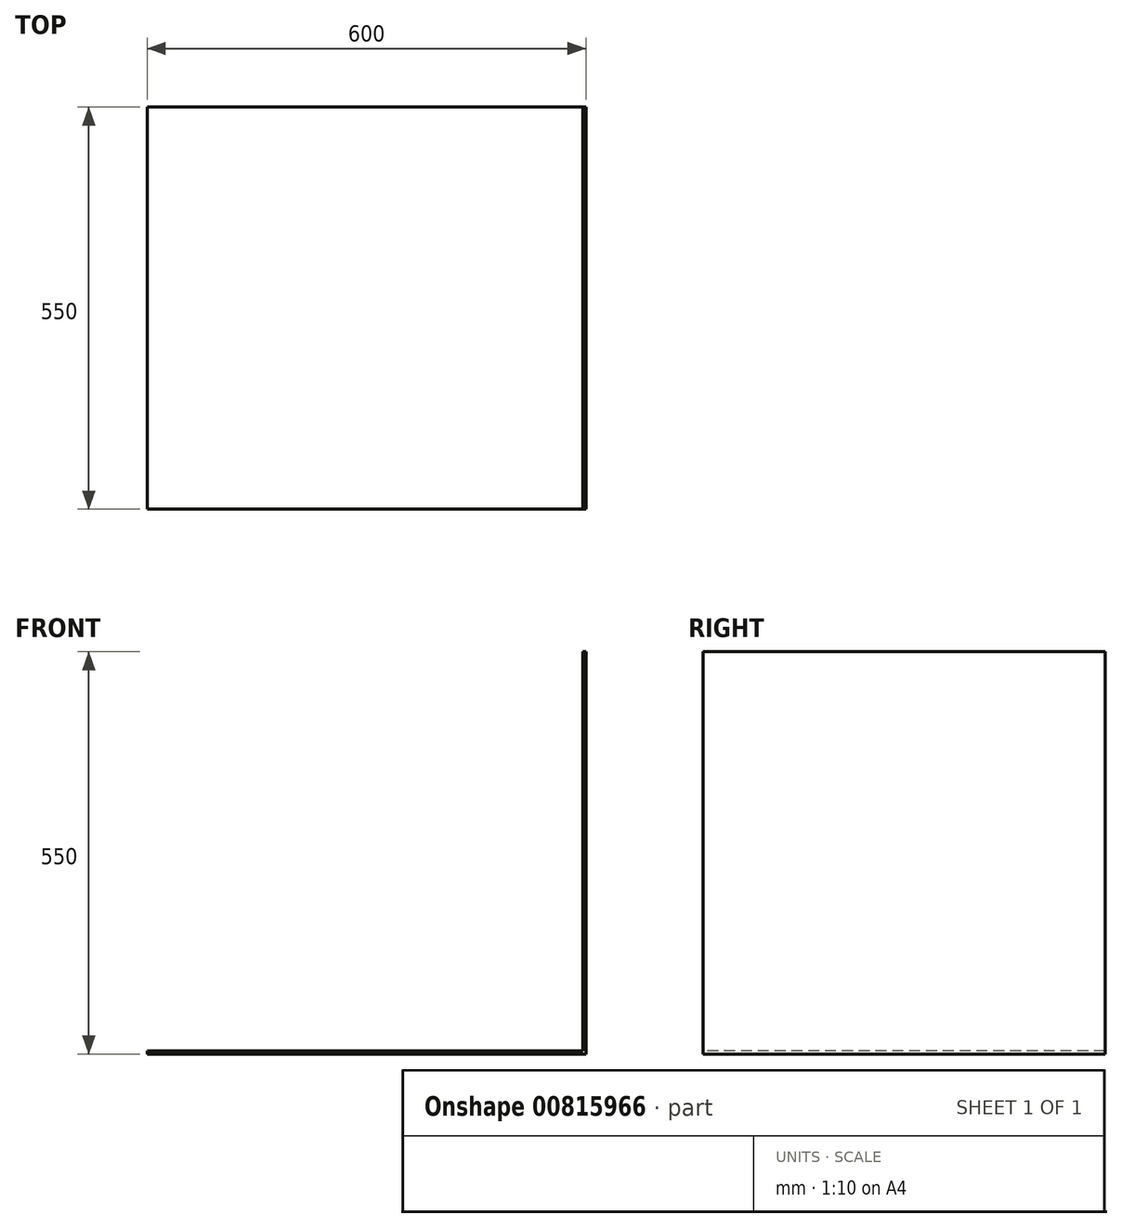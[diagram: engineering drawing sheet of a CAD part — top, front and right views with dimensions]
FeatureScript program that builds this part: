
annotation { "Feature Type Name" : "Feature", "Feature Type Description" : "" }
export const myFeature = defineFeature(function(context is Context, id is Id, definition is map)
    precondition{}
    {
        {
            var Q0;
            Q0=qCreatedBy(makeId("Front.planeOp"),FACE);
            var sketch = newSketch(context, id + "F0", { "sketchPlane" : qUnion([Q0])});
            skLineSegment(sketch, "E0", {"start": v(0, 0) * mm, "end": v(600, 0) * mm});
            skLineSegment(sketch, "E1", {"start": v(600, 0) * mm, "end": v(600, 550) * mm});
            skLineSegment(sketch, "E2.0", {"start": v(596, 4) * mm, "end": v(596, 550) * mm});
            skLineSegment(sketch, "E2.1", {"start": v(0, 4) * mm, "end": v(596, 4) * mm});
            skLineSegment(sketch, "E3", {"start": v(0, 0) * mm, "end": v(0, 4) * mm});
            skLineSegment(sketch, "E4", {"start": v(596, 550) * mm, "end": v(600, 550) * mm});
            skSolve(sketch);
        }
        {
            var Q0;
            Q0=qSketchRegion(id+"F0",true);
            extrude(context, id + "F1", {"entities" : qUnion([Q0]), "oppositeDirection" : true, "depth" : 550 * mm, "offsetDistance" : 25.4 * mm});
        }
    });
